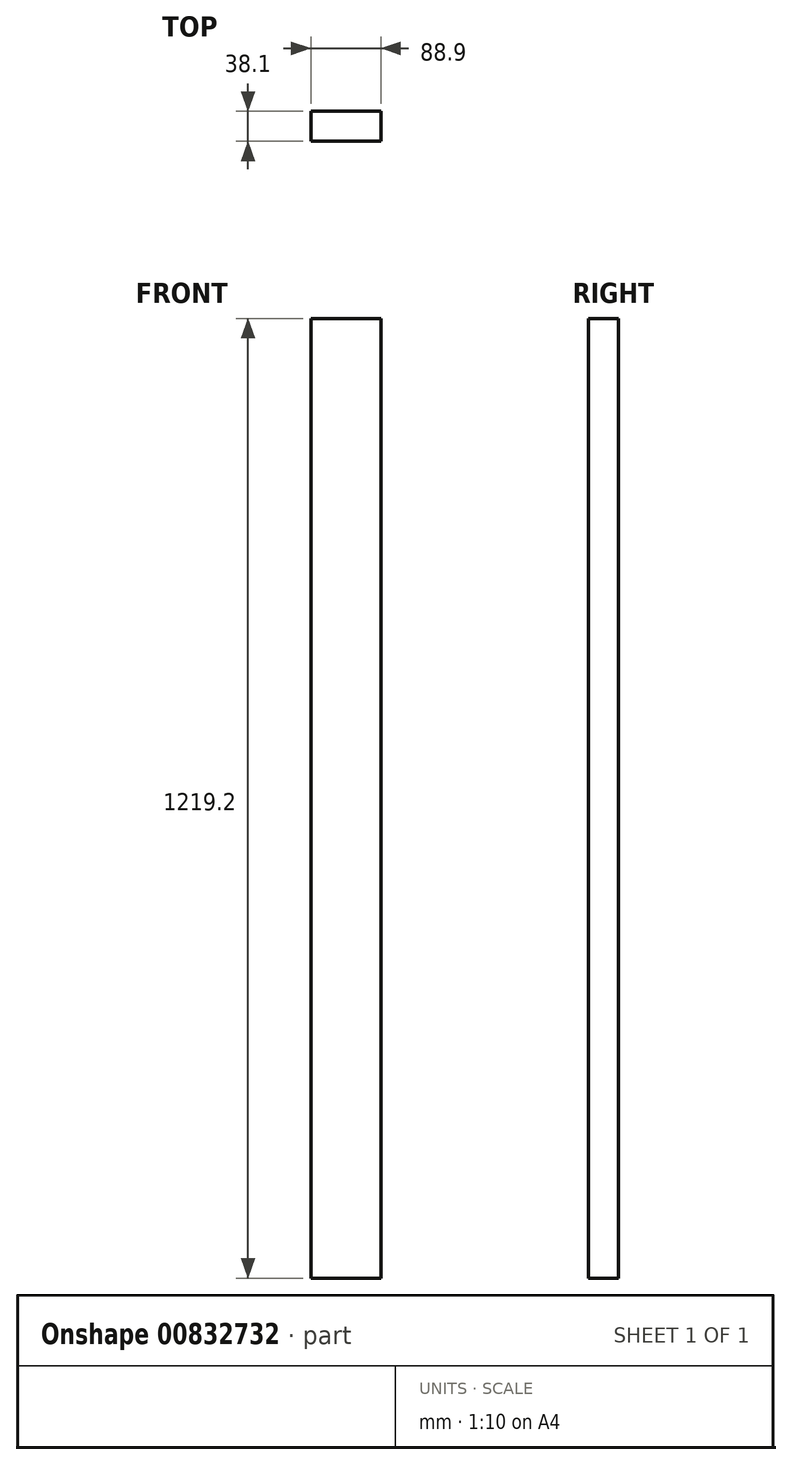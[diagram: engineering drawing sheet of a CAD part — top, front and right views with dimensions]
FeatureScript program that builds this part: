
annotation { "Feature Type Name" : "Feature", "Feature Type Description" : "" }
export const myFeature = defineFeature(function(context is Context, id is Id, definition is map)
    precondition{}
    {
        {
            var Q0;
            Q0=qCreatedBy(makeId("Front.planeOp"),FACE);
            var sketch = newSketch(context, id + "F0", { "sketchPlane" : qUnion([Q0])});
            skLineSegment(sketch, "E0.bottom", {"start": v(0, 0) * mm, "end": v(88.9, 0) * mm});
            skLineSegment(sketch, "E0.top", {"start": v(0, 1219.2) * mm, "end": v(88.9, 1219.2) * mm});
            skLineSegment(sketch, "E0.left", {"start": v(0, 0) * mm, "end": v(0, 1219.2) * mm});
            skLineSegment(sketch, "E0.right", {"start": v(88.9, 0) * mm, "end": v(88.9, 1219.2) * mm});
            skSolve(sketch);
        }
        {
            var Q0;
            Q0=makeQuery(id+"F0.imprint","IMPRINT",FACE,{"disambiguationData":[TD([[makeQuery(id+"F0.imprint","IMPRINT",EDGE,{"derivedFrom":sQuery(id+"F0.wireOp",EDGE,"E0.bottom")}),1.0]])]});
            extrude(context, id + "F1", {"entities" : qUnion([Q0]), "oppositeDirection" : true, "depth" : 38.1 * mm, "offsetDistance" : 25.4 * mm});
        }
    });
